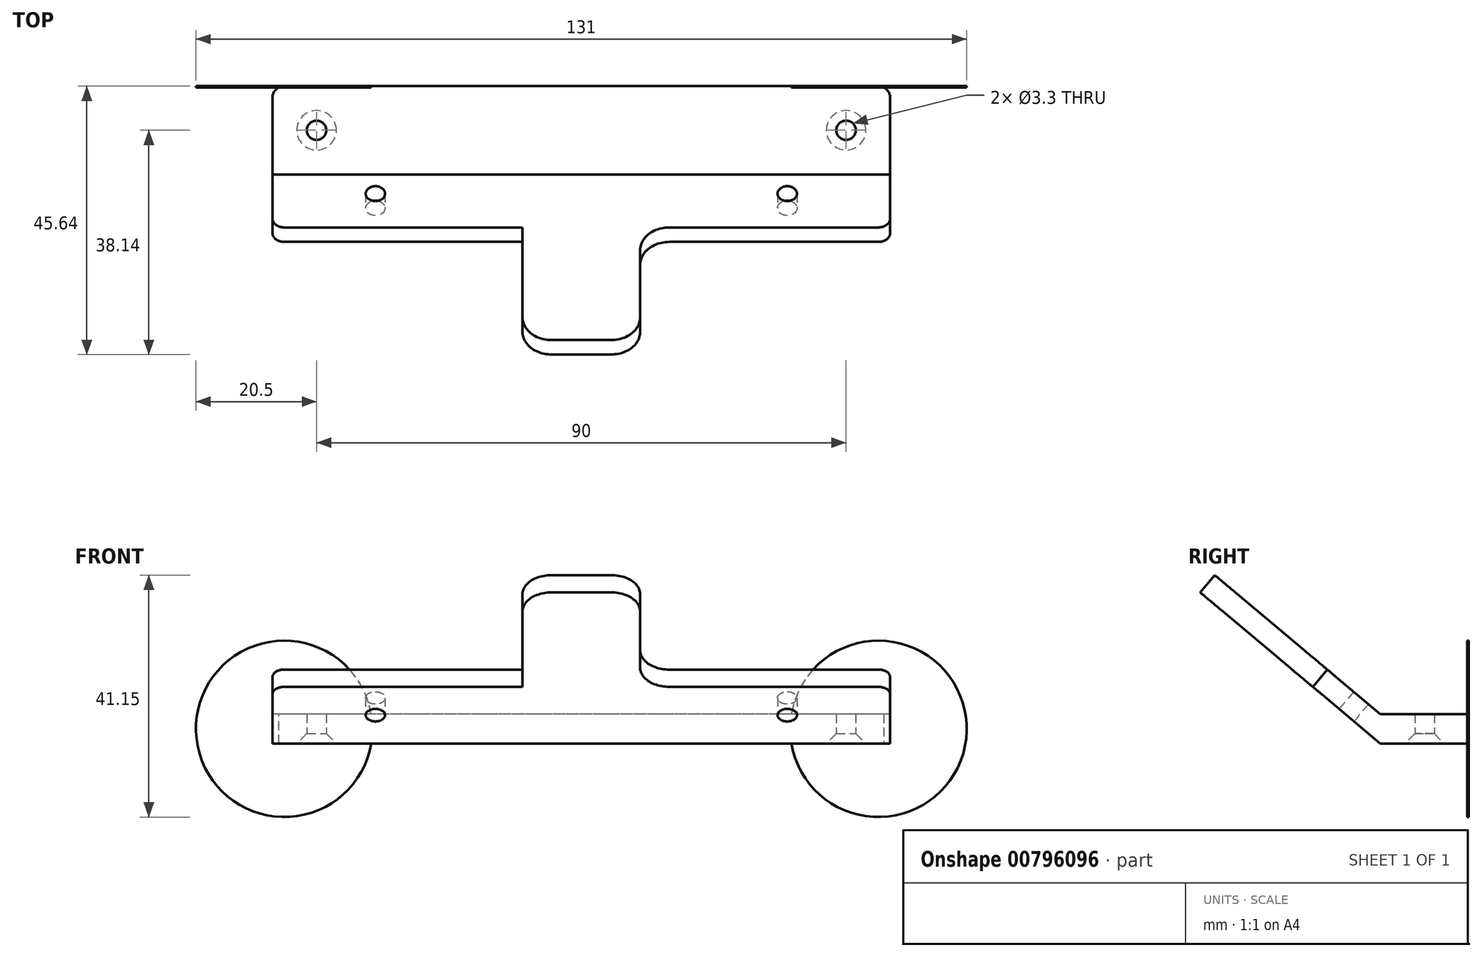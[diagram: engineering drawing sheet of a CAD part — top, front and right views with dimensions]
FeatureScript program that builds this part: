
annotation { "Feature Type Name" : "Feature", "Feature Type Description" : "" }
export const myFeature = defineFeature(function(context is Context, id is Id, definition is map)
    precondition{}
    {
        {
            var Q0;
            Q0=qCreatedBy(makeId("Right.planeOp"),FACE);
            var sketch = newSketch(context, id + "F0", { "sketchPlane" : qUnion([Q0])});
            skLineSegment(sketch, "E0", {"start": v(0, 0) * mm, "end": v(-11.5, 9.64) * mm});
            skLineSegment(sketch, "E1", {"start": v(-11.5, 9.64) * mm, "end": v(-9.03, 12.58) * mm});
            skLineSegment(sketch, "E2", {"start": v(-9.03, 12.58) * mm, "end": v(0, 5) * mm});
            skLineSegment(sketch, "E3", {"start": v(0, 5) * mm, "end": v(15, 5) * mm});
            skLineSegment(sketch, "E4", {"start": v(15, 5) * mm, "end": v(15, 0) * mm});
            skLineSegment(sketch, "E5", {"start": v(15, 0) * mm, "end": v(0, 0) * mm});
            skSolve(sketch);
        }
        {
            var Q0;
            Q0 = qSketchRegion(id + "F0", true);
            extrude(context, id + "F1", {"entities" : qUnion([Q0]), "depth" : 105 * mm, "offsetDistance" : 25 * mm});
        }
        {
            var Q0;
            Q0=makeQuery(id+"F1.opExtrude","SWEPT_FACE",FACE,{"disambiguationData":[OSD([sQuery(id+"F0.wireOp",EDGE,"E5")])]});
            var sketch = newSketch(context, id + "F2", { "sketchPlane" : qUnion([Q0])});
            skPoint(sketch, "E6.centerSnap0", {"position": v(0, -7.5) * mm});
            skPoint(sketch, "E7.centerSnap0", {"position": v(105, -7.5) * mm});
            skPoint(sketch, "E8", {"position": v(7.5, -7.5) * mm});
            skPoint(sketch, "E9", {"position": v(97.5, -7.5) * mm});
            skSolve(sketch);
        }
        {
            var Q0;
            Q0=makeQuery(id+"F1.opExtrude","CAP_EDGE",EDGE,{"disambiguationData":[OSD([sQuery(id+"F0.wireOp",EDGE,"E4")])],"isStart":true});
            var Q1;
            Q1=makeQuery(id+"F1.opExtrude","CAP_EDGE",EDGE,{"disambiguationData":[OSD([sQuery(id+"F0.wireOp",EDGE,"E4")])],"isStart":false});
            var Q2;
            Q2=makeQuery(id+"F1.opExtrude","CAP_EDGE",EDGE,{"disambiguationData":[OSD([sQuery(id+"F0.wireOp",EDGE,"E1")])],"isStart":false});
            var Q3;
            Q3=makeQuery(id+"F1.opExtrude","CAP_EDGE",EDGE,{"disambiguationData":[OSD([sQuery(id+"F0.wireOp",EDGE,"E1")])],"isStart":true});
            fillet(context, id + "F3", {"entities" : qUnion([Q0, Q1, Q2, Q3]), "radius" : 2 * mm, "tangentPropagation" : true, "allowEdgeOverflow" : false});
        }
        {
            var Q0;
            Q0=sQuery(id+"F2.wireOp",VERTEX,"E8");
            var Q1;
            Q1=sQuery(id+"F2.wireOp",VERTEX,"E9");
            var Q2;
            Q2=makeQuery(id+"F1.opExtrude","SWEPT_BODY",BODY,{"disambiguationData":[OSD([sQuery(id+"F0.wireOp",EDGE,"E0"),sQuery(id+"F0.wireOp",EDGE,"E1"),sQuery(id+"F0.wireOp",EDGE,"E2"),sQuery(id+"F0.wireOp",EDGE,"E3"),sQuery(id+"F0.wireOp",EDGE,"E4"),sQuery(id+"F0.wireOp",EDGE,"E5")])]});
            hole(context, id + "F4", {"style" : HoleStyle.C_SINK, "endStyle" : HoleEndStyle.BLIND, "standardTappedOrClearance" : lookupTablePath({ "standard" : "ISO", "fit" : "Normal", "size" : "M3", "type" : "Clearance" }), "standardBlindInLast" : lookupTablePath({ "fit" : "Standard", "standard" : "ISO", "size" : "M3", "type" : "Clearance" }), "holeDiameter" : 3.3 * mm, "cSinkDiameter" : 6.72 * mm, "cSinkAngle" : 90 * degree, "majorDiameter" : 5 * mm, "holeDepth" : 15 * mm, "isTappedThrough" : true, "tappedDepth" : 12 * mm, "tapClearance" : 3, "locations" : qUnion([Q0, Q1]), "scope" : qUnion([Q2])});
        }
        {
            var Q0;
            Q0=makeQuery(id+"F1.opExtrude","SWEPT_FACE",FACE,{"disambiguationData":[OSD([sQuery(id+"F0.wireOp",EDGE,"E0")])]});
            var sketch = newSketch(context, id + "F5", { "sketchPlane" : qUnion([Q0])});
            skLineSegment(sketch, "E10", {"start": v(0, 7.5) * mm, "end": v(105, 7.5) * mm, "construction": true});
            skPoint(sketch, "E11", {"position": v(17.5, 7.5) * mm});
            skPoint(sketch, "E12", {"position": v(87.5, 7.5) * mm});
            skLineSegment(sketch, "E13", {"start": v(52.5, 0) * mm, "end": v(52.5, 15) * mm, "construction": true});
            skSolve(sketch);
        }
        {
            var Q0;
            Q0=sQuery(id+"F5.wireOp",VERTEX,"E11");
            var Q1;
            Q1=sQuery(id+"F5.wireOp",VERTEX,"E12");
            var Q2;
            Q2=makeQuery(id+"F1.opExtrude","SWEPT_BODY",BODY,{"disambiguationData":[OSD([sQuery(id+"F0.wireOp",EDGE,"E0"),sQuery(id+"F0.wireOp",EDGE,"E1"),sQuery(id+"F0.wireOp",EDGE,"E2"),sQuery(id+"F0.wireOp",EDGE,"E3"),sQuery(id+"F0.wireOp",EDGE,"E4"),sQuery(id+"F0.wireOp",EDGE,"E5")])]});
            hole(context, id + "F6", {"style" : HoleStyle.SIMPLE, "endStyle" : HoleEndStyle.BLIND, "standardTappedOrClearance" : lookupTablePath({ "standard" : "ISO", "fit" : "Normal", "size" : "M3", "type" : "Clearance" }), "standardBlindInLast" : lookupTablePath({ "fit" : "Standard", "standard" : "ISO", "size" : "M3", "type" : "Clearance" }), "holeDiameter" : 3.3 * mm, "majorDiameter" : 5 * mm, "holeDepth" : 15 * mm, "isTappedThrough" : true, "tappedDepth" : 12 * mm, "tapClearance" : 3, "locations" : qUnion([Q0, Q1]), "scope" : qUnion([Q2])});
        }
        {
            var Q0;
            Q0=makeQuery(id+"F1.opExtrude","SWEPT_FACE",FACE,{"disambiguationData":[OSD([sQuery(id+"F0.wireOp",EDGE,"E1")])]});
            var sketch = newSketch(context, id + "F7", { "sketchPlane" : qUnion([Q0])});
            skLineSegment(sketch, "E14.bottom", {"start": v(62.5, 3.83) * mm, "end": v(42.5, 3.83) * mm});
            skLineSegment(sketch, "E14.top", {"start": v(62.5, 0) * mm, "end": v(42.5, 0) * mm});
            skLineSegment(sketch, "E14.left", {"start": v(62.5, 3.83) * mm, "end": v(62.5, 0) * mm});
            skLineSegment(sketch, "E14.right", {"start": v(42.5, 3.83) * mm, "end": v(42.5, 0) * mm});
            skPoint(sketch, "E14.middle", {"position": v(52.5, 1.92) * mm});
            skPoint(sketch, "E14.middle.positionSnap0", {"position": v(2, 1.92) * mm});
            skPoint(sketch, "E14.middle.positionSnap1", {"position": v(52.5, 3.83) * mm});
            skPoint(sketch, "E14.centerSnap0", {"position": v(2, 1.92) * mm});
            skPoint(sketch, "E14.centerSnap1", {"position": v(52.5, 3.83) * mm});
            skSolve(sketch);
        }
        {
            var Q0;
            Q0 = qSketchRegion(id + "F7", true);
            extrude(context, id + "F8", {"entities" : qUnion([Q0]), "operationType" : NewBodyOperationType.ADD, "depth" : 25 * mm, "offsetDistance" : 25 * mm});
        }
        {
            var Q0;
            Q0=makeQuery(id+"F8.opExtrude","CAP_EDGE",EDGE,{"disambiguationData":[OSD([sQuery(id+"F7.wireOp",EDGE,"E14.right")])],"isStart":true});
            var Q1;
            Q1=makeQuery(id+"F8.opExtrude","CAP_EDGE",EDGE,{"disambiguationData":[OSD([sQuery(id+"F7.wireOp",EDGE,"E14.left")])],"isStart":true});
            var Q2;
            Q2=makeQuery(id+"F8.opExtrude","CAP_EDGE",EDGE,{"disambiguationData":[OSD([sQuery(id+"F7.wireOp",EDGE,"E14.left")])],"isStart":false});
            var Q3;
            Q3=makeQuery(id+"F8.opExtrude","CAP_EDGE",EDGE,{"disambiguationData":[OSD([sQuery(id+"F7.wireOp",EDGE,"E14.right")])],"isStart":false});
            fillet(context, id + "F9", {"entities" : qUnion([Q0, Q1, Q2, Q3]), "radius" : 5 * mm, "tangentPropagation" : true, "allowEdgeOverflow" : false});
        }
        {
            var Q0;
            Q0=makeQuery(id+"F1.opExtrude","SWEPT_FACE",FACE,{"disambiguationData":[OSD([sQuery(id+"F0.wireOp",EDGE,"E4")])]});
            var sketch = newSketch(context, id + "F10", { "sketchPlane" : qUnion([Q0])});
            skCircle(sketch, "E15", {"center": v(-103, 2.5) * mm, "radius": 15 * mm});
            skCircle(sketch, "E16", {"center": v(-2, 2.5) * mm, "radius": 15 * mm});
            skSolve(sketch);
        }
        {
            var Q0;
            {var subQ1=sQuery(id+"F0.wireOp",EDGE,"E4");var subQ6=makeQuery(id+"F3.opFillet","BLEND_EDGE",EDGE,{"blendedFrom":[makeQuery(id+"F1.opExtrude","CAP_EDGE",EDGE,{"disambiguationData":[OSD([subQ1])],"isStart":true}),makeQuery(id+"F1.opExtrude","SWEPT_FACE",FACE,{"disambiguationData":[OSD([subQ1])]})],"blendedInto":[makeQuery(id+"F1.opExtrude","SWEPT_FACE",FACE,{"disambiguationData":[OSD([subQ1])]})]});Q0=makeQuery(id+"F10.imprint","IMPRINT",FACE,{"disambiguationData":[TD([[makeQuery(id+"F10.imprint","IMPRINT",EDGE,{"derivedFrom":subQ6}),-1.0]])]});}
            var Q1;
            {var subQ1=sQuery(id+"F0.wireOp",EDGE,"E4");var subQ6=makeQuery(id+"F3.opFillet","BLEND_EDGE",EDGE,{"blendedFrom":[makeQuery(id+"F1.opExtrude","CAP_EDGE",EDGE,{"disambiguationData":[OSD([subQ1])],"isStart":false}),makeQuery(id+"F1.opExtrude","SWEPT_FACE",FACE,{"disambiguationData":[OSD([subQ1])]})],"blendedInto":[makeQuery(id+"F1.opExtrude","SWEPT_FACE",FACE,{"disambiguationData":[OSD([subQ1])]})]});Q1=makeQuery(id+"F10.imprint","IMPRINT",FACE,{"disambiguationData":[TD([[makeQuery(id+"F10.imprint","IMPRINT",EDGE,{"derivedFrom":subQ6}),-1.0]])]});}
            extrude(context, id + "F11", {"entities" : qUnion([Q0, Q1]), "operationType" : NewBodyOperationType.ADD, "oppositeDirection" : true, "depth" : .22 * mm, "offsetDistance" : 25 * mm});
        }
    });
